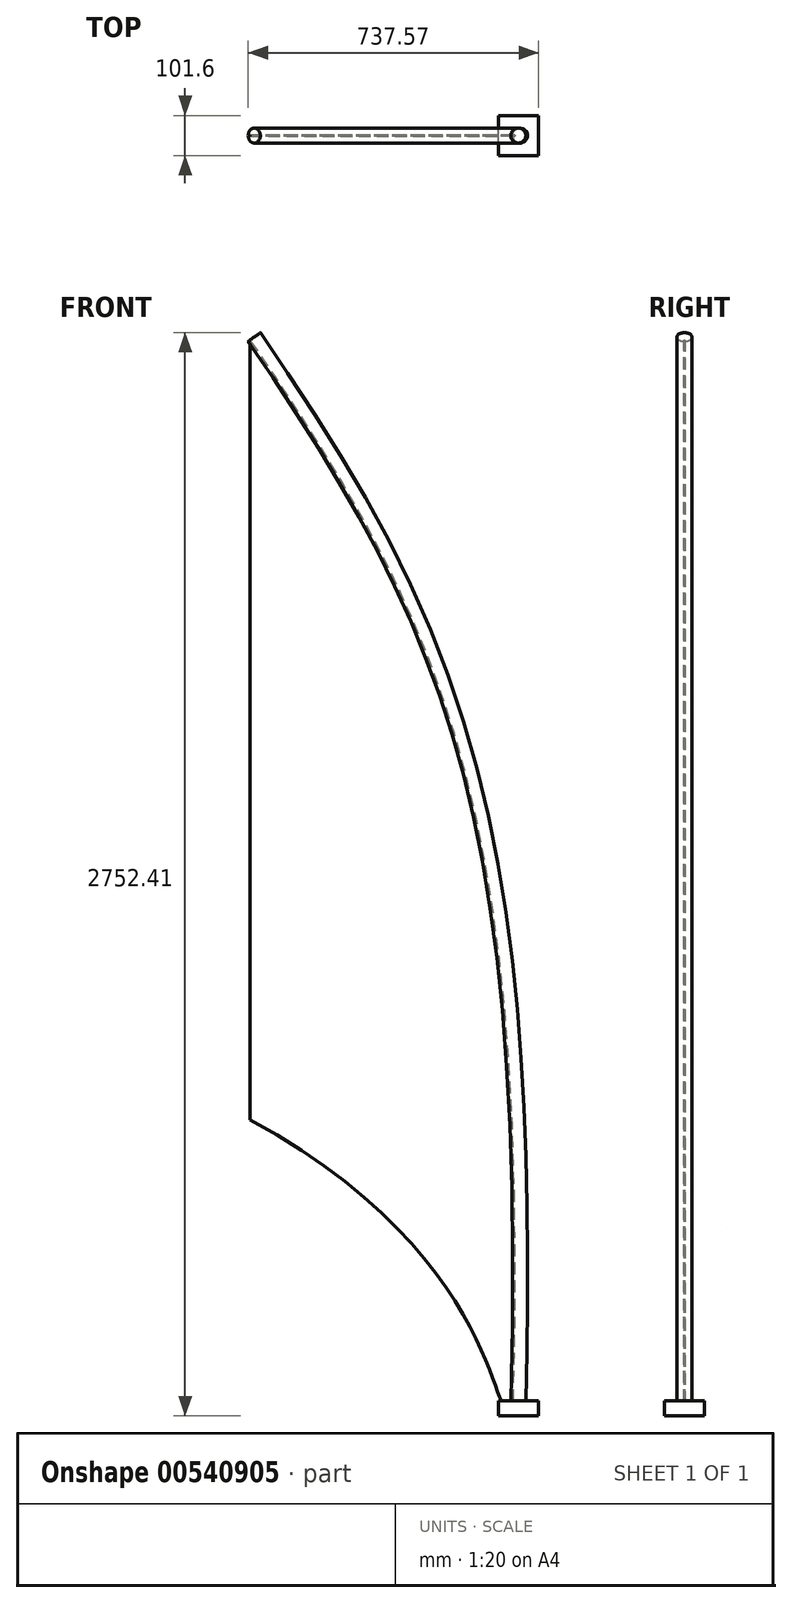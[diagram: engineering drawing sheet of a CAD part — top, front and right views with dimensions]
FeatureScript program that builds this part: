
annotation { "Feature Type Name" : "Feature", "Feature Type Description" : "" }
export const myFeature = defineFeature(function(context is Context, id is Id, definition is map)
    precondition{}
    {
        {
            var Q0;
            Q0=qCreatedBy(makeId("Front.planeOp"),FACE);
            var sketch = newSketch(context, id + "F0", { "sketchPlane" : qUnion([Q0])});
            skPoint(sketch, "E0", {"position": v(668.57, -714.52) * mm});
            skPoint(sketch, "E1", {"position": v(637.78, -714.52) * mm});
            skLineSegment(sketch, "E2", {"start": v(668.57, -714.52) * mm, "end": v(637.78, -714.52) * mm});
            skPoint(sketch, "E3", {"position": v(0, 1981.2) * mm});
            skLineSegment(sketch, "E4", {"start": v(0, 1981.2) * mm, "end": v(0, 0) * mm});
            skFitSpline(sketch, "E5", {"points": [v(0, 0) * mm, v(637.78, -714.52) * mm], "startDerivative": vector(1615, -879.91) * mm, "endDerivative": vector(93.1, -194.18) * mm});
            skFitSpline(sketch, "E6", {"points": [v(668.57, -714.52) * mm, v(0, 1981.2) * mm], "startDerivative": vector(117.03, 4536.9) * mm, "endDerivative": vector(-1474.56, 2156.71) * mm});
            skSolve(sketch);
        }
        {
            var Q0;
            Q0 = qSketchRegion(id + "F0", true);
            extrude(context, id + "F1", {"entities" : qUnion([Q0]), "depth" : 2.54 * mm, "offsetDistance" : 25.4 * mm});
        }
        {
            var Q0;
            Q0=makeQuery(id+"F1.opExtrude","SWEPT_FACE",FACE,{"disambiguationData":[OSD([sQuery(id+"F0.wireOp",EDGE,"E2")])]});
            var sketch = newSketch(context, id + "F2", { "sketchPlane" : qUnion([Q0])});
            skLineSegment(sketch, "E7", {"start": v(668.57, 1.27) * mm, "end": v(681.27, 1.27) * mm, "construction": true});
            skPoint(sketch, "E7.endSnap0", {"position": v(668.57, 1.27) * mm});
            skCircle(sketch, "E8", {"center": v(681.27, 1.27) * mm, "radius": 19.05 * mm});
            skSolve(sketch);
        }
        {
            var Q0;
            {var subQ1=sQuery(id+"F0.wireOp",EDGE,"E2");var subQ6=makeQuery(id+"F1.opExtrude","SWEPT_EDGE",EDGE,{"disambiguationData":[OSD([subQ1,sQuery(id+"F0.wireOp",EDGE,"E6")])]});Q0=makeQuery(id+"F2.imprint","IMPRINT",FACE,{"disambiguationData":[TD([[makeQuery(id+"F2.imprint","IMPRINT",EDGE,{"derivedFrom":subQ6}),1.0]])]});}
            var Q1;
            Q1=makeQuery(id+"F1.opExtrude","CAP_EDGE",EDGE,{"disambiguationData":[OSD([sQuery(id+"F0.wireOp",EDGE,"E6")])],"isStart":false});
            sweep(context, id + "F3", {"profiles" : qUnion([Q0]), "path" : qUnion([Q1])});
        }
        {
            var Q0;
            Q0=makeQuery(id+"F3.opSweep","CAP_FACE",FACE,{"disambiguationData":[OSD([sQuery(id+"F0.wireOp",EDGE,"E2"),sQuery(id+"F0.wireOp",EDGE,"E6"),sQuery(id+"F2.wireOp",EDGE,"E8")])],"isStart":true});
            var sketch = newSketch(context, id + "F4", { "sketchPlane" : qUnion([Q0])});
            skArc(sketch, "E9.0.0", {"start": v(662.26, 2.54) * mm, "mid": v(700.32, 1.27) * mm, "end": v(662.26, 0) * mm});
            skLineSegment(sketch, "E9.0.1", {"start": v(662.26, 2.54) * mm, "end": v(668.57, 2.54) * mm});
            skLineSegment(sketch, "E9.0.2", {"start": v(668.57, 0) * mm, "end": v(668.57, 2.54) * mm});
            skLineSegment(sketch, "E9.0.3", {"start": v(662.26, 0) * mm, "end": v(668.57, 0) * mm});
            skLineSegment(sketch, "E10.bottom", {"start": v(630.86, 52.07) * mm, "end": v(732.46, 52.07) * mm});
            skLineSegment(sketch, "E10.top", {"start": v(630.86, -49.53) * mm, "end": v(732.46, -49.53) * mm});
            skLineSegment(sketch, "E10.left", {"start": v(630.86, 52.07) * mm, "end": v(630.86, -49.53) * mm});
            skLineSegment(sketch, "E10.right", {"start": v(732.46, 52.07) * mm, "end": v(732.46, -49.53) * mm});
            skPoint(sketch, "E10.middle", {"position": v(681.66, 1.27) * mm});
            skSolve(sketch);
        }
        {
            var Q0;
            Q0=makeQuery(id+"F4.imprint","IMPRINT",FACE,{"disambiguationData":[TD([[makeQuery(id+"F4.imprint","IMPRINT",EDGE,{"derivedFrom":sQuery(id+"F4.wireOp",EDGE,"E9.0.0")}),1.0]])]});
            var Q1;
            Q1=makeQuery(id+"F4.imprint","IMPRINT",FACE,{"disambiguationData":[TD([[makeQuery(id+"F4.imprint","IMPRINT",EDGE,{"derivedFrom":sQuery(id+"F4.wireOp",EDGE,"E9.0.0")}),-1.0]])]});
            extrude(context, id + "F5", {"entities" : qUnion([Q0, Q1]), "depth" : 38.1 * mm, "offsetDistance" : 25.4 * mm});
        }
    });
